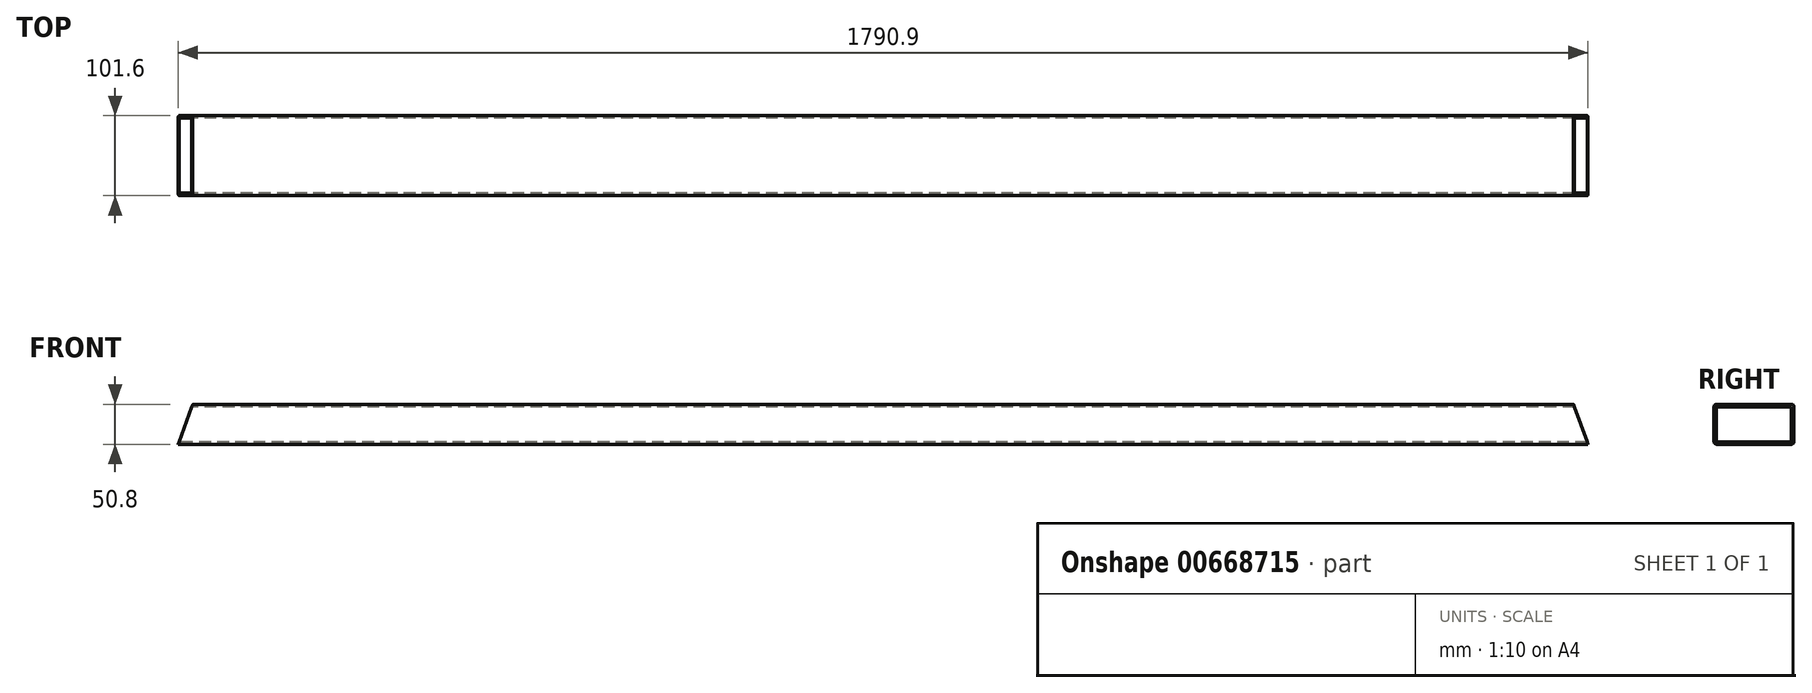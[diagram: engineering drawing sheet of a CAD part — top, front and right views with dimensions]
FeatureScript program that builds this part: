
annotation { "Feature Type Name" : "Feature", "Feature Type Description" : "" }
export const myFeature = defineFeature(function(context is Context, id is Id, definition is map)
    precondition{}
    {
        {
            var Q0;
            Q0=qCreatedBy(makeId("Right.planeOp"),FACE);
            var sketch = newSketch(context, id + "F0", { "sketchPlane" : qUnion([Q0])});
            skLineSegment(sketch, "E0.bottom", {"start": v(47.63, 25.4) * mm, "end": v(-47.62, 25.4) * mm});
            skLineSegment(sketch, "E0.top", {"start": v(47.63, -25.4) * mm, "end": v(-47.62, -25.4) * mm});
            skLineSegment(sketch, "E0.left", {"start": v(50.8, 22.23) * mm, "end": v(50.8, -22.23) * mm});
            skLineSegment(sketch, "E0.right", {"start": v(-50.8, 22.22) * mm, "end": v(-50.8, -22.23) * mm});
            skPoint(sketch, "E0.middle", {"position": v(0, 0) * mm});
            skPoint(sketch, "E1.visualSharp", {"position": v(-50.8, 25.4) * mm});
            skArc(sketch, "E1.filletArc", {"start": v(-47.63, 25.4) * mm, "mid": v(-49.87, 24.47) * mm, "end": v(-50.8, 22.22) * mm});
            skPoint(sketch, "E2.visualSharp", {"position": v(50.8, 25.4) * mm});
            skArc(sketch, "E2.filletArc", {"start": v(50.8, 22.23) * mm, "mid": v(49.87, 24.47) * mm, "end": v(47.63, 25.4) * mm});
            skPoint(sketch, "E3.visualSharp", {"position": v(-50.8, -25.4) * mm});
            skArc(sketch, "E3.filletArc", {"start": v(-50.8, -22.23) * mm, "mid": v(-49.87, -24.47) * mm, "end": v(-47.62, -25.4) * mm});
            skPoint(sketch, "E4.visualSharp", {"position": v(50.8, -25.4) * mm});
            skArc(sketch, "E4.filletArc", {"start": v(47.63, -25.4) * mm, "mid": v(49.87, -24.47) * mm, "end": v(50.8, -22.23) * mm});
            skLineSegment(sketch, "E5.0", {"start": v(47.62, 22.23) * mm, "end": v(-47.62, 22.23) * mm});
            skLineSegment(sketch, "E5.1", {"start": v(47.62, 22.23) * mm, "end": v(47.63, -22.23) * mm});
            skLineSegment(sketch, "E5.2", {"start": v(47.63, -22.23) * mm, "end": v(-47.62, -22.23) * mm});
            skLineSegment(sketch, "E5.3", {"start": v(-47.62, 22.23) * mm, "end": v(-47.62, -22.23) * mm});
            skSolve(sketch);
        }
        {
            var Q0;
            Q0=qSketchRegion(id+"F0",true);
            extrude(context, id + "F1", {"entities" : qUnion([Q0]), "depth" : 1790.9 * mm});
        }
        {
            var Q0;
            Q0=makeQuery(id+"F1.opExtrude","SWEPT_FACE",FACE,{"disambiguationData":[OSD([sQuery(id+"F0.wireOp",EDGE,"E0.right")])]});
            var sketch = newSketch(context, id + "F2", { "sketchPlane" : qUnion([Q0])});
            skLineSegment(sketch, "E6.bottom", {"start": v(18.49, 25.4) * mm, "end": v(0, 25.4) * mm});
            skLineSegment(sketch, "E6.right", {"start": v(0, 25.4) * mm, "end": v(0, -25.4) * mm});
            skPoint(sketch, "E6.middle", {"position": v(9.24, 0) * mm});
            skLineSegment(sketch, "E7", {"start": v(0, -25.4) * mm, "end": v(18.49, 25.4) * mm});
            skPoint(sketch, "E6.top.start.orphan", {"position": v(18.49, -25.4) * mm});
            skLineSegment(sketch, "E8.bottom", {"start": v(1790.9, 25.4) * mm, "end": v(1772.41, 25.4) * mm});
            skLineSegment(sketch, "E8.left", {"start": v(1790.9, 25.4) * mm, "end": v(1790.9, -25.4) * mm});
            skPoint(sketch, "E8.middle", {"position": v(1781.66, 0) * mm});
            skLineSegment(sketch, "E9", {"start": v(1772.41, 25.4) * mm, "end": v(1790.9, -25.4) * mm});
            skPoint(sketch, "E8.top.end.orphan", {"position": v(1772.41, -25.4) * mm});
            skSolve(sketch);
        }
        {
            var Q0;
            Q0=qSketchRegion(id+"F2",true);
            extrude(context, id + "F3", {"entities" : qUnion([Q0]), "operationType" : NewBodyOperationType.REMOVE, "endBound" : BoundingType.THROUGH_ALL, "oppositeDirection" : true, "depth" : 25.4 * mm});
        }
    });
